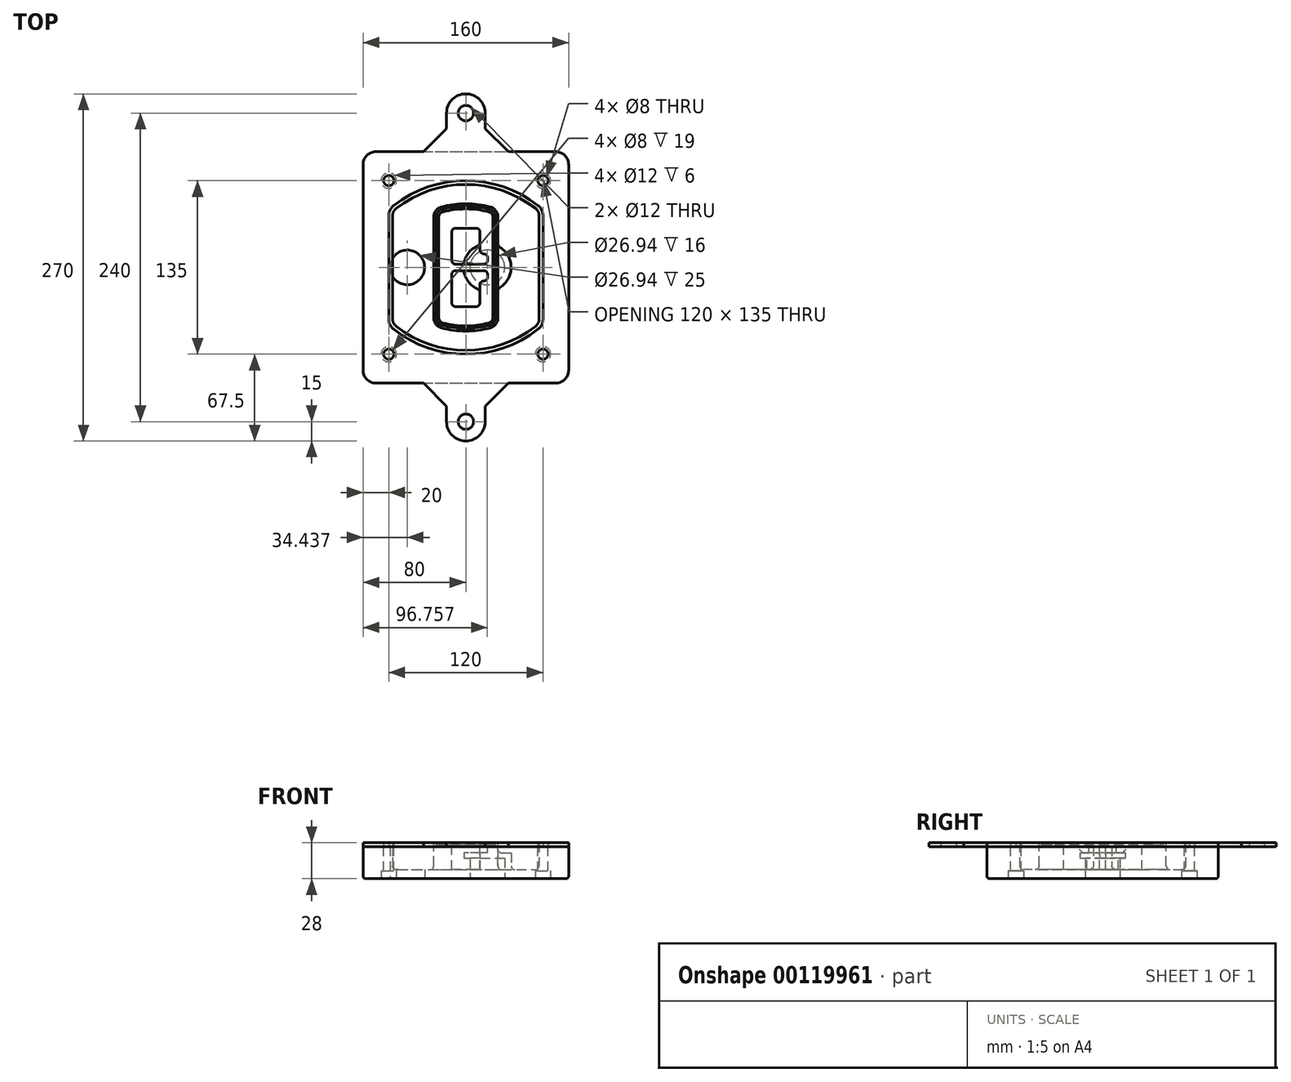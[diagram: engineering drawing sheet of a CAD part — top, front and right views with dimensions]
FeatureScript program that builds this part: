
annotation { "Feature Type Name" : "Feature", "Feature Type Description" : "" }
export const myFeature = defineFeature(function(context is Context, id is Id, definition is map)
    precondition{}
    {
        {
            var Q0;
            Q0=qCreatedBy(makeId("Top.planeOp"),FACE);
            var sketch = newSketch(context, id + "F0", { "sketchPlane" : qUnion([Q0])});
            skPoint(sketch, "E0.rect.middle", {"position": v(0, 0) * mm});
            skLineSegment(sketch, "E1.bottom", {"start": v(-70, -90) * mm, "end": v(70, -90) * mm});
            skLineSegment(sketch, "E1.top", {"start": v(-70, 90) * mm, "end": v(70, 90) * mm});
            skLineSegment(sketch, "E1.left", {"start": v(-80, -80) * mm, "end": v(-80, 80) * mm});
            skLineSegment(sketch, "E1.right", {"start": v(80, -80) * mm, "end": v(80, 80) * mm});
            skLineSegment(sketch, "E2", {"start": v(-80, 90) * mm, "end": v(80, -90) * mm, "construction": true});
            skLineSegment(sketch, "E3", {"start": v(80, 90) * mm, "end": v(-80, -90) * mm, "construction": true});
            skCircle(sketch, "E4", {"center": v(-60, 67.5) * mm, "radius": 4 * mm});
            skCircle(sketch, "E5", {"center": v(60, 67.5) * mm, "radius": 4 * mm});
            skCircle(sketch, "E6", {"center": v(60, -67.5) * mm, "radius": 4 * mm});
            skCircle(sketch, "E7", {"center": v(-60, -67.5) * mm, "radius": 4 * mm});
            skLineSegment(sketch, "E8", {"start": v(-60, 67.5) * mm, "end": v(60, 67.5) * mm, "construction": true});
            skLineSegment(sketch, "E9", {"start": v(60, 67.5) * mm, "end": v(60, -67.5) * mm, "construction": true});
            skLineSegment(sketch, "E10", {"start": v(60, -67.5) * mm, "end": v(-60, -67.5) * mm, "construction": true});
            skLineSegment(sketch, "E11", {"start": v(-60, -67.5) * mm, "end": v(-60, 67.5) * mm, "construction": true});
            skLineSegment(sketch, "E12", {"start": v(-60, 40.3) * mm, "end": v(-60, -40.3) * mm});
            skLineSegment(sketch, "E13", {"start": v(60, 40.3) * mm, "end": v(60, -40.3) * mm});
            skArc(sketch, "E14", {"start": v(56.15, 48.18) * mm, "mid": v(0, 67.5) * mm, "end": v(-56.15, 48.18) * mm});
            skArc(sketch, "E15", {"start": v(-56.15, -48.18) * mm, "mid": v(0, -67.5) * mm, "end": v(56.15, -48.18) * mm});
            skLineSegment(sketch, "E16", {"start": v(-60, 0) * mm, "end": v(60, 0) * mm, "construction": true});
            skPoint(sketch, "E17.visualSharp", {"position": v(-60, -45) * mm});
            skArc(sketch, "E17.filletArc", {"start": v(-60, -40.3) * mm, "mid": v(-58.99, -44.68) * mm, "end": v(-56.15, -48.18) * mm});
            skPoint(sketch, "E18.visualSharp", {"position": v(-60, 45) * mm});
            skArc(sketch, "E18.filletArc", {"start": v(-56.15, 48.18) * mm, "mid": v(-58.99, 44.68) * mm, "end": v(-60, 40.3) * mm});
            skPoint(sketch, "E19.visualSharp", {"position": v(60, 45) * mm});
            skArc(sketch, "E19.filletArc", {"start": v(60, 40.3) * mm, "mid": v(58.99, 44.68) * mm, "end": v(56.15, 48.18) * mm});
            skPoint(sketch, "E20.visualSharp", {"position": v(60, -45) * mm});
            skArc(sketch, "E20.filletArc", {"start": v(56.15, -48.18) * mm, "mid": v(58.99, -44.68) * mm, "end": v(60, -40.3) * mm});
            skPoint(sketch, "E21.visualSharp", {"position": v(-80, 90) * mm});
            skArc(sketch, "E21.filletArc", {"start": v(-70, 90) * mm, "mid": v(-77.07, 87.07) * mm, "end": v(-80, 80) * mm});
            skPoint(sketch, "E22.visualSharp", {"position": v(80, 90) * mm});
            skArc(sketch, "E22.filletArc", {"start": v(80, 80) * mm, "mid": v(77.07, 87.07) * mm, "end": v(70, 90) * mm});
            skPoint(sketch, "E23.visualSharp", {"position": v(80, -90) * mm});
            skArc(sketch, "E23.filletArc", {"start": v(70, -90) * mm, "mid": v(77.07, -87.07) * mm, "end": v(80, -80) * mm});
            skPoint(sketch, "E24.visualSharp", {"position": v(-80, -90) * mm});
            skArc(sketch, "E24.filletArc", {"start": v(-80, -80) * mm, "mid": v(-77.07, -87.07) * mm, "end": v(-70, -90) * mm});
            skArc(sketch, "E25.0", {"start": v(57, 40.3) * mm, "mid": v(56.3, 43.36) * mm, "end": v(54.3, 45.81) * mm});
            skLineSegment(sketch, "E25.1", {"start": v(57, 40.3) * mm, "end": v(57, -40.3) * mm});
            skArc(sketch, "E25.2", {"start": v(54.3, -45.81) * mm, "mid": v(56.3, -43.36) * mm, "end": v(57, -40.3) * mm});
            skArc(sketch, "E25.3", {"start": v(-54.3, -45.81) * mm, "mid": v(0, -64.5) * mm, "end": v(54.3, -45.81) * mm});
            skArc(sketch, "E25.4", {"start": v(-57, -40.3) * mm, "mid": v(-56.3, -43.36) * mm, "end": v(-54.3, -45.81) * mm});
            skArc(sketch, "E25.5", {"start": v(54.3, 45.81) * mm, "mid": v(0, 64.5) * mm, "end": v(-54.3, 45.81) * mm});
            skLineSegment(sketch, "E25.6", {"start": v(-57, 40.3) * mm, "end": v(-57, -40.3) * mm});
            skArc(sketch, "E25.7", {"start": v(-54.3, 45.81) * mm, "mid": v(-56.3, 43.36) * mm, "end": v(-57, 40.3) * mm});
            skArc(sketch, "E26.0", {"start": v(-58.62, 51.33) * mm, "mid": v(-62.58, 46.43) * mm, "end": v(-64, 40.3) * mm});
            skArc(sketch, "E26.1", {"start": v(58.62, 51.33) * mm, "mid": v(0, 71.5) * mm, "end": v(-58.62, 51.33) * mm});
            skArc(sketch, "E26.2", {"start": v(64, 40.3) * mm, "mid": v(62.58, 46.43) * mm, "end": v(58.62, 51.33) * mm});
            skLineSegment(sketch, "E26.3", {"start": v(64, 40.3) * mm, "end": v(64, -40.3) * mm});
            skArc(sketch, "E26.4", {"start": v(58.62, -51.33) * mm, "mid": v(62.58, -46.43) * mm, "end": v(64, -40.3) * mm});
            skLineSegment(sketch, "E26.5", {"start": v(-64, 40.3) * mm, "end": v(-64, -40.3) * mm});
            skArc(sketch, "E26.6", {"start": v(-58.62, -51.33) * mm, "mid": v(0, -71.5) * mm, "end": v(58.62, -51.33) * mm});
            skArc(sketch, "E26.7", {"start": v(-64, -40.3) * mm, "mid": v(-62.58, -46.43) * mm, "end": v(-58.62, -51.33) * mm});
            skSolve(sketch);
        }
        {
            var Q0;
            Q0=makeQuery(id+"F0.imprint","IMPRINT",FACE,{"disambiguationData":[TD([[makeQuery(id+"F0.imprint","IMPRINT",EDGE,{"derivedFrom":sQuery(id+"F0.wireOp",EDGE,"E1.bottom")}),1.0]])]});
            var Q1;
            Q1=makeQuery(id+"F0.imprint","IMPRINT",FACE,{"disambiguationData":[TD([[makeQuery(id+"F0.imprint","IMPRINT",EDGE,{"derivedFrom":sQuery(id+"F0.wireOp",EDGE,"E12")}),1.0]])]});
            var Q2;
            Q2=makeQuery(id+"F0.imprint","IMPRINT",FACE,{"disambiguationData":[TD([[makeQuery(id+"F0.imprint","IMPRINT",EDGE,{"derivedFrom":sQuery(id+"F0.wireOp",EDGE,"E25.0")}),1.0]])]});
            var Q3;
            Q3=makeQuery(id+"F0.imprint","IMPRINT",FACE,{"disambiguationData":[TD([[makeQuery(id+"F0.imprint","IMPRINT",EDGE,{"derivedFrom":sQuery(id+"F0.wireOp",EDGE,"E12")}),-1.0]])]});
            extrude(context, id + "F1", {"entities" : qUnion([Q0, Q1, Q2, Q3]), "oppositeDirection" : true, "depth" : 25 * mm});
        }
        {
            var Q0;
            Q0=makeQuery(id+"F0.imprint","IMPRINT",FACE,{"disambiguationData":[TD([[makeQuery(id+"F0.imprint","IMPRINT",EDGE,{"derivedFrom":sQuery(id+"F0.wireOp",EDGE,"E12")}),1.0]])]});
            extrude(context, id + "F2", {"entities" : qUnion([Q0]), "operationType" : NewBodyOperationType.ADD, "depth" : 3 * mm});
        }
        {
            var Q0;
            Q0=makeQuery(id+"F0.imprint","IMPRINT",FACE,{"disambiguationData":[TD([[makeQuery(id+"F0.imprint","IMPRINT",EDGE,{"derivedFrom":sQuery(id+"F0.wireOp",EDGE,"E25.0")}),1.0]])]});
            extrude(context, id + "F3", {"entities" : qUnion([Q0]), "operationType" : NewBodyOperationType.REMOVE, "oppositeDirection" : true, "depth" : 18 * mm});
        }
        {
            var Q0;
            Q0=makeQuery(id+"F2.opExtrude","CAP_FACE",FACE,{"disambiguationData":[OSD([sQuery(id+"F0.wireOp",EDGE,"E12"),sQuery(id+"F0.wireOp",EDGE,"E13"),sQuery(id+"F0.wireOp",EDGE,"E14"),sQuery(id+"F0.wireOp",EDGE,"E15"),sQuery(id+"F0.wireOp",EDGE,"E17.filletArc"),sQuery(id+"F0.wireOp",EDGE,"E18.filletArc"),sQuery(id+"F0.wireOp",EDGE,"E19.filletArc"),sQuery(id+"F0.wireOp",EDGE,"E20.filletArc"),sQuery(id+"F0.wireOp",EDGE,"E25.0"),sQuery(id+"F0.wireOp",EDGE,"E25.1"),sQuery(id+"F0.wireOp",EDGE,"E25.2"),sQuery(id+"F0.wireOp",EDGE,"E25.3"),sQuery(id+"F0.wireOp",EDGE,"E25.4"),sQuery(id+"F0.wireOp",EDGE,"E25.5"),sQuery(id+"F0.wireOp",EDGE,"E25.6"),sQuery(id+"F0.wireOp",EDGE,"E25.7")])],"isStart":false});
            var sketch = newSketch(context, id + "F4", { "sketchPlane" : qUnion([Q0])});
            skArc(sketch, "E27.0", {"start": v(-19.08, -46.97) * mm, "mid": v(0, -49.5) * mm, "end": v(19.08, -46.97) * mm});
            skArc(sketch, "E28.0", {"start": v(19.08, 46.97) * mm, "mid": v(0, 49.5) * mm, "end": v(-19.08, 46.97) * mm});
            skLineSegment(sketch, "E29", {"start": v(-25, 39.25) * mm, "end": v(-25, -39.25) * mm});
            skLineSegment(sketch, "E30", {"start": v(25, 39.25) * mm, "end": v(25, -39.25) * mm});
            skLineSegment(sketch, "E31", {"start": v(-25, 45.1) * mm, "end": v(25, 45.1) * mm, "construction": true});
            skLineSegment(sketch, "E32", {"start": v(-25, -45.1) * mm, "end": v(25, -45.1) * mm, "construction": true});
            skPoint(sketch, "E33.visualSharp", {"position": v(-25, 45.1) * mm});
            skArc(sketch, "E33.filletArc", {"start": v(-19.08, 46.97) * mm, "mid": v(-23.35, 44.11) * mm, "end": v(-25, 39.25) * mm});
            skPoint(sketch, "E34.visualSharp", {"position": v(25, 45.1) * mm});
            skArc(sketch, "E34.filletArc", {"start": v(25, 39.25) * mm, "mid": v(23.35, 44.11) * mm, "end": v(19.08, 46.97) * mm});
            skPoint(sketch, "E35.visualSharp", {"position": v(25, -45.1) * mm});
            skArc(sketch, "E35.filletArc", {"start": v(19.08, -46.97) * mm, "mid": v(23.35, -44.11) * mm, "end": v(25, -39.25) * mm});
            skPoint(sketch, "E36.visualSharp", {"position": v(-25, -45.1) * mm});
            skArc(sketch, "E36.filletArc", {"start": v(-25, -39.25) * mm, "mid": v(-23.35, -44.11) * mm, "end": v(-19.08, -46.97) * mm});
            skArc(sketch, "E37.0", {"start": v(54.3, 45.81) * mm, "mid": v(0, 64.5) * mm, "end": v(-54.3, 45.81) * mm});
            skArc(sketch, "E37.1", {"start": v(-54.3, 45.81) * mm, "mid": v(-56.3, 43.36) * mm, "end": v(-57, 40.3) * mm});
            skLineSegment(sketch, "E37.2", {"start": v(-57, 40.3) * mm, "end": v(-57, -40.3) * mm});
            skArc(sketch, "E37.3", {"start": v(-57, -40.3) * mm, "mid": v(-56.3, -43.36) * mm, "end": v(-54.3, -45.81) * mm});
            skArc(sketch, "E37.4", {"start": v(-54.3, -45.81) * mm, "mid": v(0, -64.5) * mm, "end": v(54.3, -45.81) * mm});
            skArc(sketch, "E37.5", {"start": v(54.3, -45.81) * mm, "mid": v(56.3, -43.36) * mm, "end": v(57, -40.3) * mm});
            skLineSegment(sketch, "E37.6", {"start": v(57, 40.3) * mm, "end": v(57, -40.3) * mm});
            skArc(sketch, "E37.7", {"start": v(57, 40.3) * mm, "mid": v(56.3, 43.36) * mm, "end": v(54.3, 45.81) * mm});
            skLineSegment(sketch, "E38.0", {"start": v(23, 39.25) * mm, "end": v(23, -39.25) * mm});
            skArc(sketch, "E38.1", {"start": v(18.56, -45.04) * mm, "mid": v(21.76, -42.9) * mm, "end": v(23, -39.25) * mm});
            skArc(sketch, "E38.2", {"start": v(-18.56, -45.04) * mm, "mid": v(0, -47.5) * mm, "end": v(18.56, -45.04) * mm});
            skArc(sketch, "E38.3", {"start": v(-23, -39.25) * mm, "mid": v(-21.76, -42.9) * mm, "end": v(-18.56, -45.04) * mm});
            skLineSegment(sketch, "E38.4", {"start": v(-23, 39.25) * mm, "end": v(-23, -39.25) * mm});
            skArc(sketch, "E38.5", {"start": v(23, 39.25) * mm, "mid": v(21.76, 42.9) * mm, "end": v(18.56, 45.04) * mm});
            skArc(sketch, "E38.6", {"start": v(-18.56, 45.04) * mm, "mid": v(-21.76, 42.9) * mm, "end": v(-23, 39.25) * mm});
            skArc(sketch, "E38.7", {"start": v(18.56, 45.04) * mm, "mid": v(0, 47.5) * mm, "end": v(-18.56, 45.04) * mm});
            skArc(sketch, "E39.0", {"start": v(21, 39.25) * mm, "mid": v(20.18, 41.68) * mm, "end": v(18.04, 43.1) * mm});
            skLineSegment(sketch, "E39.1", {"start": v(21, 39.25) * mm, "end": v(21, -39.25) * mm});
            skArc(sketch, "E39.2", {"start": v(18.04, -43.1) * mm, "mid": v(20.18, -41.68) * mm, "end": v(21, -39.25) * mm});
            skArc(sketch, "E39.3", {"start": v(-18.04, -43.1) * mm, "mid": v(0, -45.5) * mm, "end": v(18.04, -43.1) * mm});
            skArc(sketch, "E39.4", {"start": v(-21, -39.25) * mm, "mid": v(-20.18, -41.68) * mm, "end": v(-18.04, -43.1) * mm});
            skArc(sketch, "E39.5", {"start": v(18.04, 43.1) * mm, "mid": v(0, 45.5) * mm, "end": v(-18.04, 43.1) * mm});
            skLineSegment(sketch, "E39.6", {"start": v(-21, 39.25) * mm, "end": v(-21, -39.25) * mm});
            skArc(sketch, "E39.7", {"start": v(-18.04, 43.1) * mm, "mid": v(-20.18, 41.68) * mm, "end": v(-21, 39.25) * mm});
            skLineSegment(sketch, "E40", {"start": v(-25, 0) * mm, "end": v(25, 0) * mm, "construction": true});
            skLineSegment(sketch, "E41", {"start": v(-11, 5.5) * mm, "end": v(-11, 27.5) * mm});
            skLineSegment(sketch, "E42", {"start": v(-8, 30.5) * mm, "end": v(8, 30.5) * mm});
            skLineSegment(sketch, "E43", {"start": v(11, 27.5) * mm, "end": v(11, 13.5) * mm});
            skLineSegment(sketch, "E44", {"start": v(14, 10.5) * mm, "end": v(14, 10.5) * mm});
            skLineSegment(sketch, "E45", {"start": v(17, 7.5) * mm, "end": v(17, 5.5) * mm});
            skLineSegment(sketch, "E46", {"start": v(14, 2.5) * mm, "end": v(-8, 2.5) * mm});
            skPoint(sketch, "E47.visualSharp", {"position": v(-11, 30.5) * mm});
            skArc(sketch, "E47.filletArc", {"start": v(-8, 30.5) * mm, "mid": v(-10.12, 29.62) * mm, "end": v(-11, 27.5) * mm});
            skPoint(sketch, "E48.visualSharp", {"position": v(11, 30.5) * mm});
            skArc(sketch, "E48.filletArc", {"start": v(11, 27.5) * mm, "mid": v(10.12, 29.62) * mm, "end": v(8, 30.5) * mm});
            skPoint(sketch, "E49.visualSharp", {"position": v(11, 10.5) * mm});
            skArc(sketch, "E49.filletArc", {"start": v(11, 13.5) * mm, "mid": v(11.88, 11.38) * mm, "end": v(14, 10.5) * mm});
            skPoint(sketch, "E50.visualSharp", {"position": v(17, 10.5) * mm});
            skArc(sketch, "E50.filletArc", {"start": v(17, 7.5) * mm, "mid": v(16.12, 9.62) * mm, "end": v(14, 10.5) * mm});
            skPoint(sketch, "E51.visualSharp", {"position": v(17, 2.5) * mm});
            skArc(sketch, "E51.filletArc", {"start": v(14, 2.5) * mm, "mid": v(16.12, 3.38) * mm, "end": v(17, 5.5) * mm});
            skPoint(sketch, "E52.visualSharp", {"position": v(-11, 2.5) * mm});
            skArc(sketch, "E52.filletArc", {"start": v(-11, 5.5) * mm, "mid": v(-10.12, 3.38) * mm, "end": v(-8, 2.5) * mm});
            skLineSegment(sketch, "E53.0.MirrorCS", {"start": v(14, -2.5) * mm, "end": v(-8, -2.5) * mm});
            skArc(sketch, "E54.0.MirrorCS", {"start": v(-11, -5.5) * mm, "mid": v(-10.12, -3.38) * mm, "end": v(-8, -2.5) * mm});
            skLineSegment(sketch, "E55.0.MirrorCS", {"start": v(-11, -5.5) * mm, "end": v(-11, -27.5) * mm});
            skArc(sketch, "E56.0.MirrorCS", {"start": v(-8, -30.5) * mm, "mid": v(-10.12, -29.62) * mm, "end": v(-11, -27.5) * mm});
            skLineSegment(sketch, "E57.0.MirrorCS", {"start": v(-8, -30.5) * mm, "end": v(8, -30.5) * mm});
            skArc(sketch, "E58.0.MirrorCS", {"start": v(11, -27.5) * mm, "mid": v(10.12, -29.62) * mm, "end": v(8, -30.5) * mm});
            skLineSegment(sketch, "E59.0.MirrorCS", {"start": v(11, -27.5) * mm, "end": v(11, -13.5) * mm});
            skArc(sketch, "E60.0.MirrorCS", {"start": v(11, -13.5) * mm, "mid": v(11.88, -11.38) * mm, "end": v(14, -10.5) * mm});
            skArc(sketch, "E61.0.MirrorCS", {"start": v(17, -7.5) * mm, "mid": v(16.12, -9.62) * mm, "end": v(14, -10.5) * mm});
            skLineSegment(sketch, "E62.0.MirrorCS", {"start": v(17, -7.5) * mm, "end": v(17, -5.5) * mm});
            skArc(sketch, "E63.0.MirrorCS", {"start": v(14, -2.5) * mm, "mid": v(16.12, -3.38) * mm, "end": v(17, -5.5) * mm});
            skSolve(sketch);
        }
        {
            var Q0;
            Q0=makeQuery(id+"F4.imprint","IMPRINT",FACE,{"disambiguationData":[TD([[makeQuery(id+"F4.imprint","IMPRINT",EDGE,{"derivedFrom":sQuery(id+"F4.wireOp",EDGE,"E27.0")}),1.0]])]});
            var Q1;
            Q1=makeQuery(id+"F4.imprint","IMPRINT",FACE,{"disambiguationData":[TD([[makeQuery(id+"F4.imprint","IMPRINT",EDGE,{"derivedFrom":sQuery(id+"F4.wireOp",EDGE,"E38.0")}),-1.0]])]});
            var Q2;
            Q2=makeQuery(id+"F4.imprint","IMPRINT",FACE,{"disambiguationData":[TD([[makeQuery(id+"F4.imprint","IMPRINT",EDGE,{"derivedFrom":sQuery(id+"F4.wireOp",EDGE,"E39.0")}),1.0]])]});
            extrude(context, id + "F5", {"entities" : qUnion([Q0, Q1, Q2]), "operationType" : NewBodyOperationType.ADD, "endBound" : BoundingType.UP_TO_NEXT, "oppositeDirection" : true, "depth" : 25 * mm});
        }
        {
            var Q0;
            Q0=makeQuery(id+"F4.imprint","IMPRINT",FACE,{"disambiguationData":[TD([[makeQuery(id+"F4.imprint","IMPRINT",EDGE,{"derivedFrom":sQuery(id+"F4.wireOp",EDGE,"E38.0")}),-1.0]])]});
            extrude(context, id + "F6", {"entities" : qUnion([Q0]), "operationType" : NewBodyOperationType.REMOVE, "oppositeDirection" : true, "depth" : 2 * mm});
        }
        {
            var Q0;
            Q0=makeQuery(id+"F1.opExtrude","CAP_FACE",FACE,{"disambiguationData":[OSD([sQuery(id+"F0.wireOp",EDGE,"E1.bottom"),sQuery(id+"F0.wireOp",EDGE,"E1.top"),sQuery(id+"F0.wireOp",EDGE,"E1.left"),sQuery(id+"F0.wireOp",EDGE,"E1.right"),sQuery(id+"F0.wireOp",EDGE,"E4"),sQuery(id+"F0.wireOp",EDGE,"E5"),sQuery(id+"F0.wireOp",EDGE,"E6"),sQuery(id+"F0.wireOp",EDGE,"E7"),sQuery(id+"F0.wireOp",EDGE,"E21.filletArc"),sQuery(id+"F0.wireOp",EDGE,"E22.filletArc"),sQuery(id+"F0.wireOp",EDGE,"E23.filletArc"),sQuery(id+"F0.wireOp",EDGE,"E24.filletArc")])],"isStart":false});
            var sketch = newSketch(context, id + "F7", { "sketchPlane" : qUnion([Q0])});
            skCircle(sketch, "E64", {"center": v(16.76, 0) * mm, "radius": 13.47 * mm});
            skCircle(sketch, "E65", {"center": v(-45.56, 0) * mm, "radius": 13.47 * mm});
            skLineSegment(sketch, "E66", {"start": v(80, 0) * mm, "end": v(-80, 0) * mm});
            skCircle(sketch, "E67", {"center": v(16.76, 0) * mm, "radius": 18.47 * mm});
            skCircle(sketch, "E68", {"center": v(60, -67.5) * mm, "radius": 6 * mm});
            skCircle(sketch, "E69", {"center": v(-60, -67.5) * mm, "radius": 6 * mm});
            skCircle(sketch, "E70", {"center": v(-60, 67.5) * mm, "radius": 6 * mm});
            skCircle(sketch, "E71", {"center": v(60, 67.5) * mm, "radius": 6 * mm});
            skSolve(sketch);
        }
        {
            var Q0;
            {var subQ1=sQuery(id+"F7.wireOp",EDGE,"E66");var subQ4=sQuery(id+"F7.wireOp",EDGE,"E64");var subQ6=makeQuery(id+"F7.imprint","INTERSECT",VERTEX,{"disambiguationData":[OD(0.0)],"derivedFrom":[subQ4,subQ1]});Q0=makeQuery(id+"F7.imprint","IMPRINT",FACE,{"disambiguationData":[TD([[makeQuery(id+"F7.imprint","IMPRINT",EDGE,{"disambiguationData":[TD([[subQ6,-1.0]])],"derivedFrom":subQ4}),-1.0]])]});}
            var Q1;
            {var subQ0=sQuery(id+"F7.wireOp",EDGE,"E66");var subQ1=sQuery(id+"F7.wireOp",EDGE,"E64");var subQ3=makeQuery(id+"F7.imprint","INTERSECT",VERTEX,{"disambiguationData":[OD(0.0)],"derivedFrom":[subQ1,subQ0]});Q1=makeQuery(id+"F7.imprint","IMPRINT",FACE,{"disambiguationData":[TD([[makeQuery(id+"F7.imprint","IMPRINT",EDGE,{"disambiguationData":[TD([[subQ3,-1.0]])],"derivedFrom":subQ1}),1.0]])]});}
            var Q2;
            {var subQ0=sQuery(id+"F7.wireOp",EDGE,"E66");var subQ1=sQuery(id+"F7.wireOp",EDGE,"E64");var subQ3=makeQuery(id+"F7.imprint","INTERSECT",VERTEX,{"disambiguationData":[OD(0.0)],"derivedFrom":[subQ1,subQ0]});Q2=makeQuery(id+"F7.imprint","IMPRINT",FACE,{"disambiguationData":[TD([[makeQuery(id+"F7.imprint","IMPRINT",EDGE,{"disambiguationData":[TD([[subQ3,1.0]])],"derivedFrom":subQ1}),1.0]])]});}
            var Q3;
            {var subQ1=sQuery(id+"F7.wireOp",EDGE,"E66");var subQ4=sQuery(id+"F7.wireOp",EDGE,"E64");var subQ6=makeQuery(id+"F7.imprint","INTERSECT",VERTEX,{"disambiguationData":[OD(0.0)],"derivedFrom":[subQ4,subQ1]});Q3=makeQuery(id+"F7.imprint","IMPRINT",FACE,{"disambiguationData":[TD([[makeQuery(id+"F7.imprint","IMPRINT",EDGE,{"disambiguationData":[TD([[subQ6,1.0]])],"derivedFrom":subQ4}),-1.0]])]});}
            extrude(context, id + "F8", {"entities" : qUnion([Q0, Q1, Q2, Q3]), "operationType" : NewBodyOperationType.ADD, "oppositeDirection" : true, "depth" : 20 * mm});
        }
        {
            var Q0;
            {var subQ0=sQuery(id+"F7.wireOp",EDGE,"E66");var subQ1=sQuery(id+"F7.wireOp",EDGE,"E64");var subQ3=makeQuery(id+"F7.imprint","INTERSECT",VERTEX,{"disambiguationData":[OD(0.0)],"derivedFrom":[subQ1,subQ0]});Q0=makeQuery(id+"F7.imprint","IMPRINT",FACE,{"disambiguationData":[TD([[makeQuery(id+"F7.imprint","IMPRINT",EDGE,{"disambiguationData":[TD([[subQ3,-1.0]])],"derivedFrom":subQ1}),1.0]])]});}
            var Q1;
            {var subQ0=sQuery(id+"F7.wireOp",EDGE,"E66");var subQ1=sQuery(id+"F7.wireOp",EDGE,"E64");var subQ3=makeQuery(id+"F7.imprint","INTERSECT",VERTEX,{"disambiguationData":[OD(0.0)],"derivedFrom":[subQ1,subQ0]});Q1=makeQuery(id+"F7.imprint","IMPRINT",FACE,{"disambiguationData":[TD([[makeQuery(id+"F7.imprint","IMPRINT",EDGE,{"disambiguationData":[TD([[subQ3,1.0]])],"derivedFrom":subQ1}),1.0]])]});}
            extrude(context, id + "F9", {"entities" : qUnion([Q0, Q1]), "operationType" : NewBodyOperationType.REMOVE, "oppositeDirection" : true, "depth" : 16 * mm});
        }
        {
            var Q0;
            {var subQ0=sQuery(id+"F7.wireOp",EDGE,"E66");var subQ1=sQuery(id+"F7.wireOp",EDGE,"E65");var subQ3=makeQuery(id+"F7.imprint","INTERSECT",VERTEX,{"disambiguationData":[OD(0.0)],"derivedFrom":[subQ1,subQ0]});Q0=makeQuery(id+"F7.imprint","IMPRINT",FACE,{"disambiguationData":[TD([[makeQuery(id+"F7.imprint","IMPRINT",EDGE,{"disambiguationData":[TD([[subQ3,-1.0]])],"derivedFrom":subQ1}),1.0]])]});}
            var Q1;
            {var subQ0=sQuery(id+"F7.wireOp",EDGE,"E66");var subQ1=sQuery(id+"F7.wireOp",EDGE,"E65");var subQ3=makeQuery(id+"F7.imprint","INTERSECT",VERTEX,{"disambiguationData":[OD(0.0)],"derivedFrom":[subQ1,subQ0]});Q1=makeQuery(id+"F7.imprint","IMPRINT",FACE,{"disambiguationData":[TD([[makeQuery(id+"F7.imprint","IMPRINT",EDGE,{"disambiguationData":[TD([[subQ3,1.0]])],"derivedFrom":subQ1}),1.0]])]});}
            extrude(context, id + "F10", {"entities" : qUnion([Q0, Q1]), "operationType" : NewBodyOperationType.REMOVE, "oppositeDirection" : true, "depth" : 25 * mm});
        }
        {
            var Q0;
            Q0=makeQuery(id+"F7.imprint","IMPRINT",FACE,{"disambiguationData":[TD([[makeQuery(id+"F7.imprint","IMPRINT",EDGE,{"derivedFrom":sQuery(id+"F7.wireOp",EDGE,"E68")}),1.0]])]});
            var Q1;
            Q1=makeQuery(id+"F7.imprint","IMPRINT",FACE,{"disambiguationData":[TD([[makeQuery(id+"F7.imprint","IMPRINT",EDGE,{"derivedFrom":makeQuery(id+"F1.opExtrude","CAP_EDGE",EDGE,{"disambiguationData":[OSD([sQuery(id+"F0.wireOp",EDGE,"E5")])],"isStart":false})}),-1.0]])]});
            var Q2;
            Q2=makeQuery(id+"F7.imprint","IMPRINT",FACE,{"disambiguationData":[TD([[makeQuery(id+"F7.imprint","IMPRINT",EDGE,{"derivedFrom":sQuery(id+"F7.wireOp",EDGE,"E69")}),1.0]])]});
            var Q3;
            Q3=makeQuery(id+"F7.imprint","IMPRINT",FACE,{"disambiguationData":[TD([[makeQuery(id+"F7.imprint","IMPRINT",EDGE,{"derivedFrom":makeQuery(id+"F1.opExtrude","CAP_EDGE",EDGE,{"disambiguationData":[OSD([sQuery(id+"F0.wireOp",EDGE,"E4")])],"isStart":false})}),-1.0]])]});
            var Q4;
            Q4=makeQuery(id+"F7.imprint","IMPRINT",FACE,{"disambiguationData":[TD([[makeQuery(id+"F7.imprint","IMPRINT",EDGE,{"derivedFrom":sQuery(id+"F7.wireOp",EDGE,"E70")}),1.0]])]});
            var Q5;
            Q5=makeQuery(id+"F7.imprint","IMPRINT",FACE,{"disambiguationData":[TD([[makeQuery(id+"F7.imprint","IMPRINT",EDGE,{"derivedFrom":makeQuery(id+"F1.opExtrude","CAP_EDGE",EDGE,{"disambiguationData":[OSD([sQuery(id+"F0.wireOp",EDGE,"E7")])],"isStart":false})}),-1.0]])]});
            var Q6;
            Q6=makeQuery(id+"F7.imprint","IMPRINT",FACE,{"disambiguationData":[TD([[makeQuery(id+"F7.imprint","IMPRINT",EDGE,{"derivedFrom":sQuery(id+"F7.wireOp",EDGE,"E71")}),1.0]])]});
            var Q7;
            Q7=makeQuery(id+"F7.imprint","IMPRINT",FACE,{"disambiguationData":[TD([[makeQuery(id+"F7.imprint","IMPRINT",EDGE,{"derivedFrom":makeQuery(id+"F1.opExtrude","CAP_EDGE",EDGE,{"disambiguationData":[OSD([sQuery(id+"F0.wireOp",EDGE,"E6")])],"isStart":false})}),-1.0]])]});
            extrude(context, id + "F11", {"entities" : qUnion([Q0, Q1, Q2, Q3, Q4, Q5, Q6, Q7]), "operationType" : NewBodyOperationType.REMOVE, "oppositeDirection" : true, "depth" : 6 * mm});
        }
        {
            var Q0;
            Q0=makeQuery(id+"F9.boolean.opBoolean","COPY",FACE,{"derivedFrom":makeQuery(id+"F9.opExtrude","CAP_FACE",FACE,{"disambiguationData":[OSD([sQuery(id+"F7.wireOp",EDGE,"E64")])],"isStart":false})});
            var sketch = newSketch(context, id + "F12", { "sketchPlane" : qUnion([Q0])});
            skArc(sketch, "E72.0", {"start": v(11, 17.55) * mm, "mid": v(2.57, 11.82) * mm, "end": v(-1.54, 2.5) * mm});
            skArc(sketch, "E72.1", {"start": v(-1.54, -2.5) * mm, "mid": v(2.57, -11.82) * mm, "end": v(11, -17.55) * mm});
            skLineSegment(sketch, "E73", {"start": v(-1.54, -2.5) * mm, "end": v(14, -2.5) * mm});
            skLineSegment(sketch, "E74.0", {"start": v(14, 2.5) * mm, "end": v(-1.54, 2.5) * mm});
            skArc(sketch, "E74.1", {"start": v(14, 2.5) * mm, "mid": v(16.12, 3.38) * mm, "end": v(17, 5.5) * mm});
            skLineSegment(sketch, "E74.2", {"start": v(17, 7.5) * mm, "end": v(17, 5.5) * mm});
            skArc(sketch, "E74.3", {"start": v(17, 7.5) * mm, "mid": v(16.12, 9.62) * mm, "end": v(14, 10.5) * mm});
            skArc(sketch, "E74.4", {"start": v(11, 13.5) * mm, "mid": v(11.88, 11.38) * mm, "end": v(14, 10.5) * mm});
            skLineSegment(sketch, "E74.5", {"start": v(11, 17.55) * mm, "end": v(11, 13.5) * mm});
            skLineSegment(sketch, "E74.7", {"start": v(14, -2.5) * mm, "end": v(-1.54, -2.5) * mm});
            skArc(sketch, "E74.8", {"start": v(14, -2.5) * mm, "mid": v(16.12, -3.38) * mm, "end": v(17, -5.5) * mm});
            skLineSegment(sketch, "E74.9", {"start": v(17, -7.5) * mm, "end": v(17, -5.5) * mm});
            skArc(sketch, "E74.10", {"start": v(17, -7.5) * mm, "mid": v(16.12, -9.62) * mm, "end": v(14, -10.5) * mm});
            skArc(sketch, "E74.11", {"start": v(11, -13.5) * mm, "mid": v(11.88, -11.38) * mm, "end": v(14, -10.5) * mm});
            skLineSegment(sketch, "E74.12", {"start": v(11, -17.55) * mm, "end": v(11, -13.5) * mm});
            skPoint(sketch, "E75.orphan", {"position": v(11, -27.5) * mm});
            skPoint(sketch, "E76.orphan", {"position": v(-8, -2.5) * mm});
            skPoint(sketch, "E77.orphan", {"position": v(-8, 2.5) * mm});
            skPoint(sketch, "E78.orphan", {"position": v(11, 27.5) * mm});
            skSolve(sketch);
        }
        {
            var Q0;
            {var subQ7=sQuery(id+"F12.wireOp",EDGE,"E72.0");var subQ14=sQuery(id+"F12.wireOp",EDGE,"E72.1");var subQ16=sQuery(id+"F12.wireOp",EDGE,"E74.1");var subQ18=sQuery(id+"F12.wireOp",EDGE,"E74.8");Q0=qUnion([makeQuery(id+"F12.imprint","IMPRINT",FACE,{"disambiguationData":[TD([[makeQuery(id+"F12.imprint","IMPRINT",EDGE,{"derivedFrom":subQ7}),1.0]])]}),makeQuery(id+"F12.imprint","IMPRINT",FACE,{"disambiguationData":[TD([[makeQuery(id+"F12.imprint","IMPRINT",EDGE,{"derivedFrom":subQ14}),1.0]])]}),makeQuery(id+"F12.imprint","IMPRINT",FACE,{"disambiguationData":[TD([[makeQuery(id+"F12.imprint","IMPRINT",EDGE,{"derivedFrom":subQ16}),1.0]])]}),makeQuery(id+"F12.imprint","IMPRINT",FACE,{"disambiguationData":[TD([[makeQuery(id+"F12.imprint","IMPRINT",EDGE,{"derivedFrom":subQ18}),-1.0]])]})]);}
            var Q1;
            Q1=makeQuery(id+"F5.boolean.opBoolean","SPLIT",FACE,{"disambiguationData":[TD([makeQuery(id+"F5.opExtrude","SWEPT_FACE",FACE,{"disambiguationData":[OSD([sQuery(id+"F4.wireOp",EDGE,"E41")])]})])],"derivedFrom":makeQuery(id+"F3.boolean.opBoolean","COPY",FACE,{"derivedFrom":makeQuery(id+"F3.opExtrude","CAP_FACE",FACE,{"disambiguationData":[OSD([sQuery(id+"F0.wireOp",EDGE,"E25.0"),sQuery(id+"F0.wireOp",EDGE,"E25.1"),sQuery(id+"F0.wireOp",EDGE,"E25.2"),sQuery(id+"F0.wireOp",EDGE,"E25.3"),sQuery(id+"F0.wireOp",EDGE,"E25.4"),sQuery(id+"F0.wireOp",EDGE,"E25.5"),sQuery(id+"F0.wireOp",EDGE,"E25.6"),sQuery(id+"F0.wireOp",EDGE,"E25.7")])],"isStart":false})})});
            extrude(context, id + "F13", {"entities" : qUnion([Q0]), "operationType" : NewBodyOperationType.REMOVE, "endBound" : BoundingType.UP_TO_SURFACE, "endBoundEntityFace" : qUnion([Q1]), "depth" : 25 * mm});
        }
        {
            var Q0;
            Q0=makeQuery(id+"F3.boolean.opBoolean","COPY",EDGE,{"derivedFrom":makeQuery(id+"F3.opExtrude","CAP_EDGE",EDGE,{"disambiguationData":[OSD([sQuery(id+"F0.wireOp",EDGE,"E25.6")])],"isStart":false})});
            var Q1;
            Q1=makeQuery(id+"F8.boolean.opBoolean","INTERSECT",EDGE,{"derivedFrom":[makeQuery(id+"F5.opExtrude","SWEPT_FACE",FACE,{"disambiguationData":[OSD([sQuery(id+"F4.wireOp",EDGE,"E30")])]}),makeQuery(id+"F8.opExtrude","CAP_FACE",FACE,{"disambiguationData":[OSD([sQuery(id+"F7.wireOp",EDGE,"E67")])],"isStart":false})]});
            var Q2;
            Q2=makeQuery(id+"F8.boolean.opBoolean","INTERSECT",EDGE,{"disambiguationData":[OD(1.0)],"derivedFrom":[makeQuery(id+"F5.opExtrude","SWEPT_FACE",FACE,{"disambiguationData":[OSD([sQuery(id+"F4.wireOp",EDGE,"E30")])]}),makeQuery(id+"F8.opExtrude","SWEPT_FACE",FACE,{"disambiguationData":[OSD([sQuery(id+"F7.wireOp",EDGE,"E67")])]})]});
            var Q3;
            {var subQ0=sQuery(id+"F4.wireOp",EDGE,"E30");Q3=makeQuery(id+"F8.boolean.opBoolean","SPLIT",EDGE,{"disambiguationData":[TD([makeQuery(id+"F5.opExtrude","SWEPT_FACE",FACE,{"disambiguationData":[OSD([sQuery(id+"F4.wireOp",EDGE,"E35.filletArc")])]})])],"derivedFrom":makeQuery(id+"F5.opExtrude","CAP_EDGE",EDGE,{"disambiguationData":[OSD([subQ0])],"isStart":false})});}
            var Q4;
            {var subQ0=sQuery(id+"F0.wireOp",EDGE,"E25.7");var subQ1=sQuery(id+"F0.wireOp",EDGE,"E25.1");var subQ2=sQuery(id+"F0.wireOp",EDGE,"E25.6");var subQ3=sQuery(id+"F0.wireOp",EDGE,"E25.5");var subQ4=sQuery(id+"F0.wireOp",EDGE,"E25.4");var subQ5=sQuery(id+"F0.wireOp",EDGE,"E25.0");var subQ6=sQuery(id+"F0.wireOp",EDGE,"E25.2");var subQ7=sQuery(id+"F0.wireOp",EDGE,"E25.3");Q4=makeQuery(id+"F8.boolean.opBoolean","INTERSECT",EDGE,{"derivedFrom":[makeQuery(id+"F5.boolean.opBoolean","SPLIT",FACE,{"disambiguationData":[TD([makeQuery(id+"F2.opExtrude","SWEPT_FACE",FACE,{"disambiguationData":[OSD([subQ5])]})])],"derivedFrom":makeQuery(id+"F3.boolean.opBoolean","COPY",FACE,{"derivedFrom":makeQuery(id+"F3.opExtrude","CAP_FACE",FACE,{"disambiguationData":[OSD([subQ5,subQ1,subQ6,subQ7,subQ4,subQ3,subQ2,subQ0])],"isStart":false})})}),makeQuery(id+"F8.opExtrude","SWEPT_FACE",FACE,{"disambiguationData":[OSD([sQuery(id+"F7.wireOp",EDGE,"E67")])]})]});}
            var Q5;
            Q5=makeQuery(id+"F8.boolean.opBoolean","INTERSECT",EDGE,{"disambiguationData":[OD(0.0)],"derivedFrom":[makeQuery(id+"F5.opExtrude","SWEPT_FACE",FACE,{"disambiguationData":[OSD([sQuery(id+"F4.wireOp",EDGE,"E30")])]}),makeQuery(id+"F8.opExtrude","SWEPT_FACE",FACE,{"disambiguationData":[OSD([sQuery(id+"F7.wireOp",EDGE,"E67")])]})]});
            fillet(context, id + "F14", {"entities" : qUnion([Q0, Q1, Q2, Q3, Q4, Q5]), "radius" : 3 * mm, "tangentPropagation" : true, "allowEdgeOverflow" : false});
        }
        {
            var Q0;
            Q0=makeQuery(id+"F1.opExtrude","CAP_EDGE",EDGE,{"disambiguationData":[OSD([sQuery(id+"F0.wireOp",EDGE,"E1.bottom")])],"isStart":false});
            fillet(context, id + "F15", {"entities" : qUnion([Q0]), "radius" : 2 * mm, "tangentPropagation" : true, "allowEdgeOverflow" : false});
        }
        {
            var Q0;
            Q0=qCreatedBy(makeId("Top.planeOp"),FACE);
            var sketch = newSketch(context, id + "F16", { "sketchPlane" : qUnion([Q0])});
            skLineSegment(sketch, "E79.0", {"start": v(-70, 90) * mm, "end": v(70, 90) * mm});
            skArc(sketch, "E79.1", {"start": v(-70, 90) * mm, "mid": v(-77.07, 87.07) * mm, "end": v(-80, 80) * mm});
            skLineSegment(sketch, "E79.2", {"start": v(-80, -80) * mm, "end": v(-80, 80) * mm});
            skArc(sketch, "E79.3", {"start": v(-80, -80) * mm, "mid": v(-77.07, -87.07) * mm, "end": v(-70, -90) * mm});
            skLineSegment(sketch, "E79.4", {"start": v(-70, -90) * mm, "end": v(70, -90) * mm});
            skArc(sketch, "E79.5", {"start": v(70, -90) * mm, "mid": v(77.07, -87.07) * mm, "end": v(80, -80) * mm});
            skLineSegment(sketch, "E79.6", {"start": v(80, -80) * mm, "end": v(80, 80) * mm});
            skArc(sketch, "E79.7", {"start": v(80, 80) * mm, "mid": v(77.07, 87.07) * mm, "end": v(70, 90) * mm});
            skCircle(sketch, "E79.8", {"center": v(60, 67.5) * mm, "radius": 4 * mm});
            skCircle(sketch, "E79.9", {"center": v(-60, 67.5) * mm, "radius": 4 * mm});
            skArc(sketch, "E79.10", {"start": v(56.15, 48.18) * mm, "mid": v(0, 67.5) * mm, "end": v(-56.15, 48.18) * mm});
            skArc(sketch, "E79.11", {"start": v(-56.15, 48.18) * mm, "mid": v(-58.99, 44.68) * mm, "end": v(-60, 40.3) * mm});
            skArc(sketch, "E79.12", {"start": v(60, 40.3) * mm, "mid": v(58.99, 44.68) * mm, "end": v(56.15, 48.18) * mm});
            skLineSegment(sketch, "E79.13", {"start": v(-60, 40.3) * mm, "end": v(-60, -40.3) * mm});
            skArc(sketch, "E79.14", {"start": v(-56.15, -48.18) * mm, "mid": v(0, -67.5) * mm, "end": v(56.15, -48.18) * mm});
            skArc(sketch, "E79.15", {"start": v(-60, -40.3) * mm, "mid": v(-58.99, -44.68) * mm, "end": v(-56.15, -48.18) * mm});
            skArc(sketch, "E79.16", {"start": v(56.15, -48.18) * mm, "mid": v(58.99, -44.68) * mm, "end": v(60, -40.3) * mm});
            skLineSegment(sketch, "E79.17", {"start": v(60, 40.3) * mm, "end": v(60, -40.3) * mm});
            skCircle(sketch, "E79.18", {"center": v(60, -67.5) * mm, "radius": 4 * mm});
            skCircle(sketch, "E79.19", {"center": v(-60, -67.5) * mm, "radius": 4 * mm});
            skLineSegment(sketch, "E80", {"start": v(-33, 90) * mm, "end": v(-15, 108) * mm});
            skLineSegment(sketch, "E81", {"start": v(-15, 108) * mm, "end": v(-15, 120) * mm});
            skLineSegment(sketch, "E82", {"start": v(33, 90) * mm, "end": v(15, 108) * mm});
            skLineSegment(sketch, "E83", {"start": v(15, 108) * mm, "end": v(15, 120) * mm});
            skArc(sketch, "E84", {"start": v(15, 120) * mm, "mid": v(0, 135) * mm, "end": v(-15, 120) * mm});
            skCircle(sketch, "E85", {"center": v(0, 120) * mm, "radius": 6 * mm});
            skLineSegment(sketch, "E86", {"start": v(0, 120) * mm, "end": v(0, 90) * mm, "construction": true});
            skLineSegment(sketch, "E87.0", {"start": v(62.93, 72.93) * mm, "end": v(-62.93, 72.93) * mm});
            skArc(sketch, "E87.1", {"start": v(-62.93, 72.93) * mm, "mid": v(-66.17, 89.24) * mm, "end": v(-80, 80) * mm});
            skArc(sketch, "E87.2", {"start": v(80, 80) * mm, "mid": v(66.17, 89.24) * mm, "end": v(62.93, 72.93) * mm});
            skLineSegment(sketch, "E88", {"start": v(-80, 0) * mm, "end": v(80, 0) * mm, "construction": true});
            skLineSegment(sketch, "E89.MirrorCS", {"start": v(-33, -90) * mm, "end": v(-15, -108) * mm});
            skLineSegment(sketch, "E90.MirrorCS", {"start": v(-15, -108) * mm, "end": v(-15, -120) * mm});
            skArc(sketch, "E91.MirrorCS", {"start": v(15, -120) * mm, "mid": v(0, -135) * mm, "end": v(-15, -120) * mm});
            skLineSegment(sketch, "E92.MirrorCS", {"start": v(33, -90) * mm, "end": v(15, -108) * mm});
            skLineSegment(sketch, "E93.MirrorCS", {"start": v(0, -120) * mm, "end": v(0, -90) * mm, "construction": true});
            skCircle(sketch, "E94.MirrorC", {"center": v(0, -120) * mm, "radius": 6 * mm});
            skLineSegment(sketch, "E95.MirrorCS", {"start": v(15, -108) * mm, "end": v(15, -120) * mm});
            skSolve(sketch);
        }
        {
            var Q0;
            Q0 = qSketchRegion(id + "F16", true);
            var Q1;
            Q1=makeQuery(id+"F2.opExtrude","CAP_FACE",FACE,{"disambiguationData":[OSD([sQuery(id+"F0.wireOp",EDGE,"E12"),sQuery(id+"F0.wireOp",EDGE,"E13"),sQuery(id+"F0.wireOp",EDGE,"E14"),sQuery(id+"F0.wireOp",EDGE,"E15"),sQuery(id+"F0.wireOp",EDGE,"E17.filletArc"),sQuery(id+"F0.wireOp",EDGE,"E18.filletArc"),sQuery(id+"F0.wireOp",EDGE,"E19.filletArc"),sQuery(id+"F0.wireOp",EDGE,"E20.filletArc"),sQuery(id+"F0.wireOp",EDGE,"E25.0"),sQuery(id+"F0.wireOp",EDGE,"E25.1"),sQuery(id+"F0.wireOp",EDGE,"E25.2"),sQuery(id+"F0.wireOp",EDGE,"E25.3"),sQuery(id+"F0.wireOp",EDGE,"E25.4"),sQuery(id+"F0.wireOp",EDGE,"E25.5"),sQuery(id+"F0.wireOp",EDGE,"E25.6"),sQuery(id+"F0.wireOp",EDGE,"E25.7")])],"isStart":false});
            extrude(context, id + "F17", {"entities" : qUnion([Q0]), "endBound" : BoundingType.UP_TO_SURFACE, "endBoundEntityFace" : qUnion([Q1]), "depth" : 25 * mm});
        }
    });
